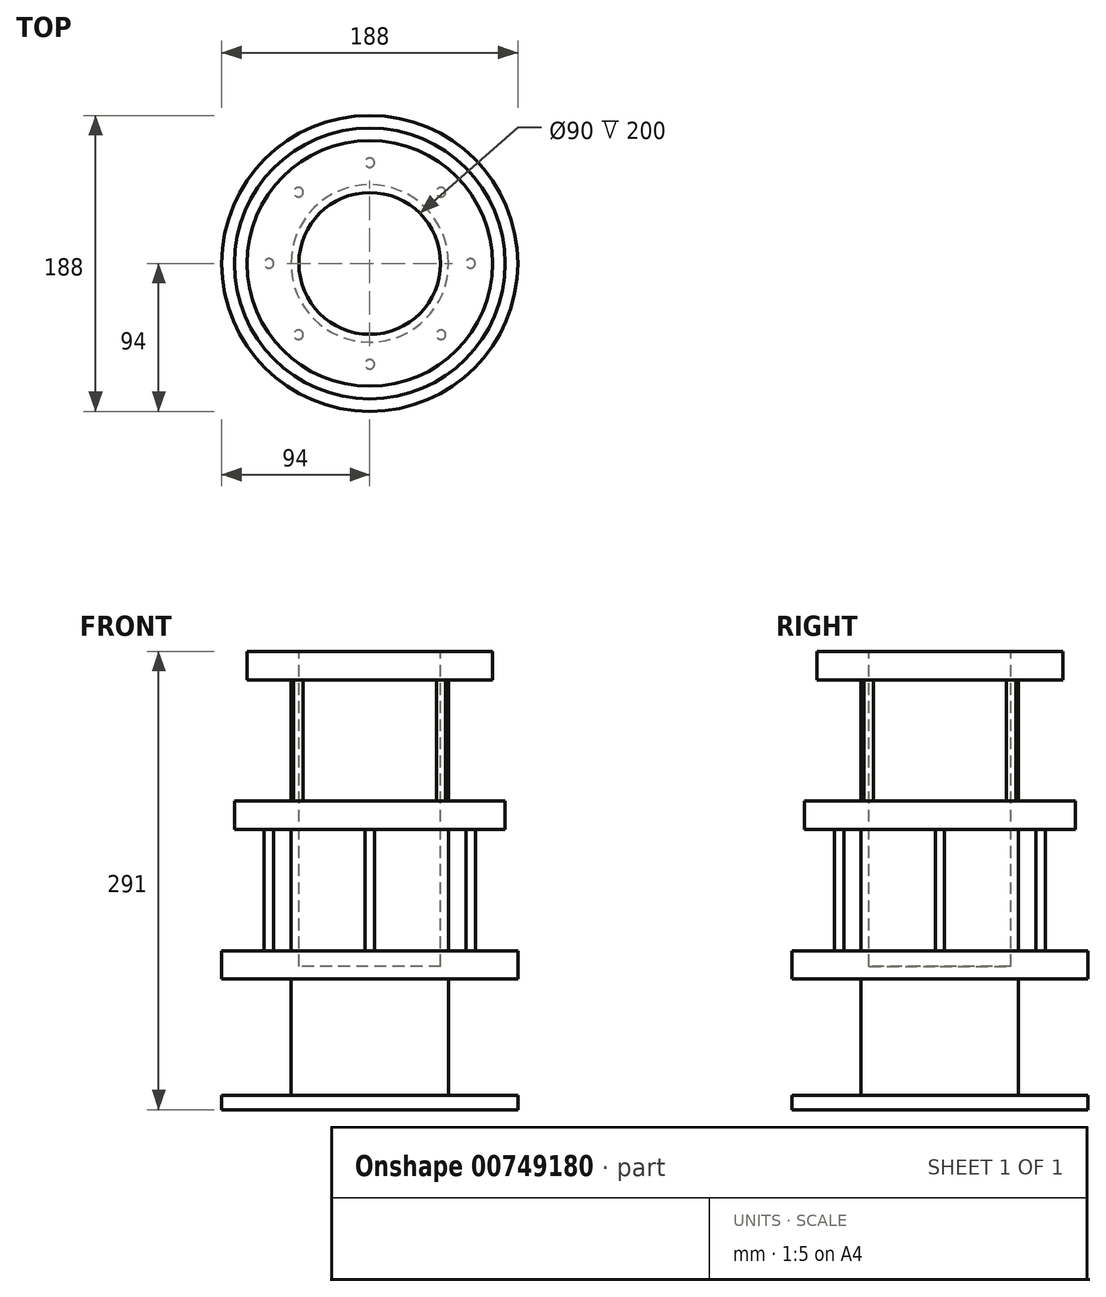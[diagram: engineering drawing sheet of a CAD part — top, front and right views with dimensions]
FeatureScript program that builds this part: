
annotation { "Feature Type Name" : "Feature", "Feature Type Description" : "" }
export const myFeature = defineFeature(function(context is Context, id is Id, definition is map)
    precondition{}
    {
        {
            var Q0;
            Q0=qCreatedBy(makeId("Top.planeOp"),FACE);
            var sketch = newSketch(context, id + "F0", { "sketchPlane" : qUnion([Q0])});
            skCircle(sketch, "E0", {"center": v(0, 0) * mm, "radius": 94 * mm});
            skSolve(sketch);
        }
        {
            var Q0;
            Q0 = qSketchRegion(id + "F0", true);
            extrude(context, id + "F1", {"entities" : qUnion([Q0]), "depth" : 9 * mm, "offsetDistance" : 25 * mm});
        }
        {
            var Q0;
            Q0=makeQuery(id+"F1.opExtrude","CAP_FACE",FACE,{"disambiguationData":[OSD([sQuery(id+"F0.wireOp",EDGE,"E0")])],"isStart":false});
            var sketch = newSketch(context, id + "F2", { "sketchPlane" : qUnion([Q0])});
            skCircle(sketch, "E1", {"center": v(0, 0) * mm, "radius": 50 * mm});
            skSolve(sketch);
        }
        {
            var Q0;
            Q0=makeQuery(id+"F2.imprint","IMPRINT",FACE,{"disambiguationData":[TD([[makeQuery(id+"F2.imprint","IMPRINT",EDGE,{"derivedFrom":sQuery(id+"F2.wireOp",EDGE,"E1")}),1.0]])]});
            extrude(context, id + "F3", {"entities" : qUnion([Q0]), "operationType" : NewBodyOperationType.ADD, "depth" : 74 * mm, "offsetDistance" : 25 * mm});
        }
        {
            var Q0;
            Q0=makeQuery(id+"F3.opExtrude","CAP_FACE",FACE,{"disambiguationData":[OSD([sQuery(id+"F2.wireOp",EDGE,"E1")])],"isStart":false});
            var sketch = newSketch(context, id + "F4", { "sketchPlane" : qUnion([Q0])});
            skCircle(sketch, "E2", {"center": v(0, 0) * mm, "radius": 94 * mm});
            skSolve(sketch);
        }
        {
            var Q0;
            Q0 = qSketchRegion(id + "F4", true);
            extrude(context, id + "F5", {"entities" : qUnion([Q0]), "operationType" : NewBodyOperationType.ADD, "depth" : 18 * mm, "offsetDistance" : 25 * mm});
        }
        {
            var Q0;
            Q0=makeQuery(id+"F5.opExtrude","CAP_FACE",FACE,{"disambiguationData":[OSD([sQuery(id+"F4.wireOp",EDGE,"E2")])],"isStart":false});
            var sketch = newSketch(context, id + "F6", { "sketchPlane" : qUnion([Q0])});
            skCircle(sketch, "E3", {"center": v(0, 0) * mm, "radius": 64 * mm});
            skCircle(sketch, "E4", {"center": v(0, 64) * mm, "radius": 3 * mm});
            skCircle(sketch, "E5", {"center": v(64, 0) * mm, "radius": 3 * mm});
            skCircle(sketch, "E6", {"center": v(0, -64) * mm, "radius": 3 * mm});
            skCircle(sketch, "E7", {"center": v(-64, 0) * mm, "radius": 3 * mm});
            skSolve(sketch);
        }
        {
            var Q0;
            {var subQ0=sQuery(id+"F6.wireOp",EDGE,"E4");var subQ1=sQuery(id+"F6.wireOp",EDGE,"E3");var subQ2=makeQuery(id+"F6.imprint","INTERSECT",VERTEX,{"disambiguationData":[OD(0.0)],"derivedFrom":[subQ1,subQ0]});Q0=makeQuery(id+"F6.imprint","IMPRINT",FACE,{"disambiguationData":[TD([[makeQuery(id+"F6.imprint","IMPRINT",EDGE,{"disambiguationData":[TD([[subQ2,-1.0]])],"derivedFrom":subQ1}),1.0]])]});}
            var Q1;
            {var subQ0=sQuery(id+"F6.wireOp",EDGE,"E4");var subQ1=sQuery(id+"F6.wireOp",EDGE,"E3");var subQ2=makeQuery(id+"F6.imprint","INTERSECT",VERTEX,{"disambiguationData":[OD(0.0)],"derivedFrom":[subQ1,subQ0]});Q1=makeQuery(id+"F6.imprint","IMPRINT",FACE,{"disambiguationData":[TD([[makeQuery(id+"F6.imprint","IMPRINT",EDGE,{"disambiguationData":[TD([[subQ2,-1.0]])],"derivedFrom":subQ1}),-1.0]])]});}
            var Q2;
            {var subQ0=sQuery(id+"F6.wireOp",EDGE,"E7");var subQ1=sQuery(id+"F6.wireOp",EDGE,"E3");var subQ2=makeQuery(id+"F6.imprint","INTERSECT",VERTEX,{"disambiguationData":[OD(0.0)],"derivedFrom":[subQ1,subQ0]});Q2=makeQuery(id+"F6.imprint","IMPRINT",FACE,{"disambiguationData":[TD([[makeQuery(id+"F6.imprint","IMPRINT",EDGE,{"disambiguationData":[TD([[subQ2,-1.0]])],"derivedFrom":subQ1}),-1.0]])]});}
            var Q3;
            {var subQ0=sQuery(id+"F6.wireOp",EDGE,"E7");var subQ1=sQuery(id+"F6.wireOp",EDGE,"E3");var subQ2=makeQuery(id+"F6.imprint","INTERSECT",VERTEX,{"disambiguationData":[OD(0.0)],"derivedFrom":[subQ1,subQ0]});Q3=makeQuery(id+"F6.imprint","IMPRINT",FACE,{"disambiguationData":[TD([[makeQuery(id+"F6.imprint","IMPRINT",EDGE,{"disambiguationData":[TD([[subQ2,-1.0]])],"derivedFrom":subQ1}),1.0]])]});}
            var Q4;
            {var subQ0=sQuery(id+"F6.wireOp",EDGE,"E6");var subQ1=sQuery(id+"F6.wireOp",EDGE,"E3");var subQ2=makeQuery(id+"F6.imprint","INTERSECT",VERTEX,{"disambiguationData":[OD(0.0)],"derivedFrom":[subQ1,subQ0]});Q4=makeQuery(id+"F6.imprint","IMPRINT",FACE,{"disambiguationData":[TD([[makeQuery(id+"F6.imprint","IMPRINT",EDGE,{"disambiguationData":[TD([[subQ2,-1.0]])],"derivedFrom":subQ1}),1.0]])]});}
            var Q5;
            {var subQ0=sQuery(id+"F6.wireOp",EDGE,"E6");var subQ1=sQuery(id+"F6.wireOp",EDGE,"E3");var subQ2=makeQuery(id+"F6.imprint","INTERSECT",VERTEX,{"disambiguationData":[OD(0.0)],"derivedFrom":[subQ1,subQ0]});Q5=makeQuery(id+"F6.imprint","IMPRINT",FACE,{"disambiguationData":[TD([[makeQuery(id+"F6.imprint","IMPRINT",EDGE,{"disambiguationData":[TD([[subQ2,-1.0]])],"derivedFrom":subQ1}),-1.0]])]});}
            var Q6;
            {var subQ0=sQuery(id+"F6.wireOp",EDGE,"E5");var subQ1=sQuery(id+"F6.wireOp",EDGE,"E3");var subQ2=makeQuery(id+"F6.imprint","INTERSECT",VERTEX,{"disambiguationData":[OD(0.0)],"derivedFrom":[subQ1,subQ0]});Q6=makeQuery(id+"F6.imprint","IMPRINT",FACE,{"disambiguationData":[TD([[makeQuery(id+"F6.imprint","IMPRINT",EDGE,{"disambiguationData":[TD([[subQ2,1.0]])],"derivedFrom":subQ1}),1.0]])]});}
            var Q7;
            {var subQ0=sQuery(id+"F6.wireOp",EDGE,"E5");var subQ1=sQuery(id+"F6.wireOp",EDGE,"E3");var subQ2=makeQuery(id+"F6.imprint","INTERSECT",VERTEX,{"disambiguationData":[OD(0.0)],"derivedFrom":[subQ1,subQ0]});Q7=makeQuery(id+"F6.imprint","IMPRINT",FACE,{"disambiguationData":[TD([[makeQuery(id+"F6.imprint","IMPRINT",EDGE,{"disambiguationData":[TD([[subQ2,1.0]])],"derivedFrom":subQ1}),-1.0]])]});}
            extrude(context, id + "F7", {"entities" : qUnion([Q0, Q1, Q2, Q3, Q4, Q5, Q6, Q7]), "operationType" : NewBodyOperationType.ADD, "depth" : 77 * mm, "offsetDistance" : 25 * mm});
        }
        {
            var Q0;
            Q0=makeQuery(id+"F5.opExtrude","CAP_FACE",FACE,{"disambiguationData":[OSD([sQuery(id+"F4.wireOp",EDGE,"E2")])],"isStart":false});
            var sketch = newSketch(context, id + "F8", { "sketchPlane" : qUnion([Q0])});
            skCircle(sketch, "E8", {"center": v(0, 0) * mm, "radius": 50 * mm});
            skSolve(sketch);
        }
        {
            var Q0;
            Q0 = qSketchRegion(id + "F8", true);
            var Q1;
            Q1=makeQuery(id+"F8.imprint","IMPRINT",FACE,{"disambiguationData":[TD([[makeQuery(id+"F8.imprint","IMPRINT",EDGE,{"derivedFrom":sQuery(id+"F8.wireOp",EDGE,"E8")}),1.0]])]});
            extrude(context, id + "F9", {"entities" : qUnion([Q0, Q1]), "operationType" : NewBodyOperationType.ADD, "depth" : 77 * mm, "offsetDistance" : 25 * mm});
        }
        {
            var Q0;
            Q0=makeQuery(id+"F9.opExtrude","CAP_FACE",FACE,{"disambiguationData":[OSD([sQuery(id+"F8.wireOp",EDGE,"E8")])],"isStart":false});
            var sketch = newSketch(context, id + "F10", { "sketchPlane" : qUnion([Q0])});
            skCircle(sketch, "E9", {"center": v(0, 0) * mm, "radius": 86 * mm});
            skSolve(sketch);
        }
        {
            var Q0;
            Q0 = qSketchRegion(id + "F10", true);
            extrude(context, id + "F11", {"entities" : qUnion([Q0]), "operationType" : NewBodyOperationType.ADD, "depth" : 18 * mm, "offsetDistance" : 25 * mm});
        }
        {
            var Q0;
            Q0=makeQuery(id+"F11.opExtrude","CAP_FACE",FACE,{"disambiguationData":[OSD([sQuery(id+"F10.wireOp",EDGE,"E9")])],"isStart":false});
            var sketch = newSketch(context, id + "F12", { "sketchPlane" : qUnion([Q0])});
            skCircle(sketch, "E10", {"center": v(-45.25, 45.25) * mm, "radius": 3 * mm});
            skCircle(sketch, "E11", {"center": v(45.25, 45.25) * mm, "radius": 3 * mm});
            skCircle(sketch, "E12", {"center": v(45.25, -45.25) * mm, "radius": 3 * mm});
            skCircle(sketch, "E13", {"center": v(-45.25, -45.25) * mm, "radius": 3 * mm});
            skSolve(sketch);
        }
        {
            var Q0;
            Q0=makeQuery(id+"F12.imprint","IMPRINT",FACE,{"disambiguationData":[TD([[makeQuery(id+"F12.imprint","IMPRINT",EDGE,{"derivedFrom":sQuery(id+"F12.wireOp",EDGE,"E10")}),1.0]])]});
            var Q1;
            Q1=makeQuery(id+"F12.imprint","IMPRINT",FACE,{"disambiguationData":[TD([[makeQuery(id+"F12.imprint","IMPRINT",EDGE,{"derivedFrom":sQuery(id+"F12.wireOp",EDGE,"E11")}),1.0]])]});
            var Q2;
            Q2=makeQuery(id+"F12.imprint","IMPRINT",FACE,{"disambiguationData":[TD([[makeQuery(id+"F12.imprint","IMPRINT",EDGE,{"derivedFrom":sQuery(id+"F12.wireOp",EDGE,"E12")}),1.0]])]});
            var Q3;
            Q3=makeQuery(id+"F12.imprint","IMPRINT",FACE,{"disambiguationData":[TD([[makeQuery(id+"F12.imprint","IMPRINT",EDGE,{"derivedFrom":sQuery(id+"F12.wireOp",EDGE,"E13")}),1.0]])]});
            extrude(context, id + "F13", {"entities" : qUnion([Q0, Q1, Q2, Q3]), "operationType" : NewBodyOperationType.ADD, "depth" : 77 * mm, "offsetDistance" : 25 * mm});
        }
        {
            var Q0;
            Q0=makeQuery(id+"F11.opExtrude","CAP_FACE",FACE,{"disambiguationData":[OSD([sQuery(id+"F10.wireOp",EDGE,"E9")])],"isStart":false});
            var sketch = newSketch(context, id + "F14", { "sketchPlane" : qUnion([Q0])});
            skCircle(sketch, "E14", {"center": v(0, 0) * mm, "radius": 50 * mm});
            skSolve(sketch);
        }
        {
            var Q0;
            Q0=makeQuery(id+"F14.imprint","IMPRINT",FACE,{"disambiguationData":[TD([[makeQuery(id+"F14.imprint","IMPRINT",EDGE,{"derivedFrom":sQuery(id+"F14.wireOp",EDGE,"E14")}),1.0]])]});
            extrude(context, id + "F15", {"entities" : qUnion([Q0]), "operationType" : NewBodyOperationType.ADD, "depth" : 77 * mm, "offsetDistance" : 25 * mm});
        }
        {
            var Q0;
            Q0=makeQuery(id+"F15.opExtrude","CAP_FACE",FACE,{"disambiguationData":[OSD([sQuery(id+"F14.wireOp",EDGE,"E14")])],"isStart":false});
            var sketch = newSketch(context, id + "F16", { "sketchPlane" : qUnion([Q0])});
            skCircle(sketch, "E15", {"center": v(0, 0) * mm, "radius": 78 * mm});
            skSolve(sketch);
        }
        {
            var Q0;
            Q0 = qSketchRegion(id + "F16", true);
            extrude(context, id + "F17", {"entities" : qUnion([Q0]), "operationType" : NewBodyOperationType.ADD, "depth" : 18 * mm, "offsetDistance" : 25 * mm});
        }
        {
            var Q0;
            Q0=makeQuery(id+"F17.opExtrude","CAP_FACE",FACE,{"disambiguationData":[OSD([sQuery(id+"F16.wireOp",EDGE,"E15")])],"isStart":false});
            var sketch = newSketch(context, id + "F18", { "sketchPlane" : qUnion([Q0])});
            skCircle(sketch, "E16", {"center": v(0, 0) * mm, "radius": 45 * mm});
            skSolve(sketch);
        }
        {
            var Q0;
            Q0=makeQuery(id+"F18.imprint","IMPRINT",FACE,{"disambiguationData":[TD([[makeQuery(id+"F18.imprint","IMPRINT",EDGE,{"derivedFrom":sQuery(id+"F18.wireOp",EDGE,"E16")}),1.0]])]});
            extrude(context, id + "F19", {"entities" : qUnion([Q0]), "operationType" : NewBodyOperationType.REMOVE, "oppositeDirection" : true, "depth" : 200 * mm, "offsetDistance" : 25 * mm});
        }
    });
